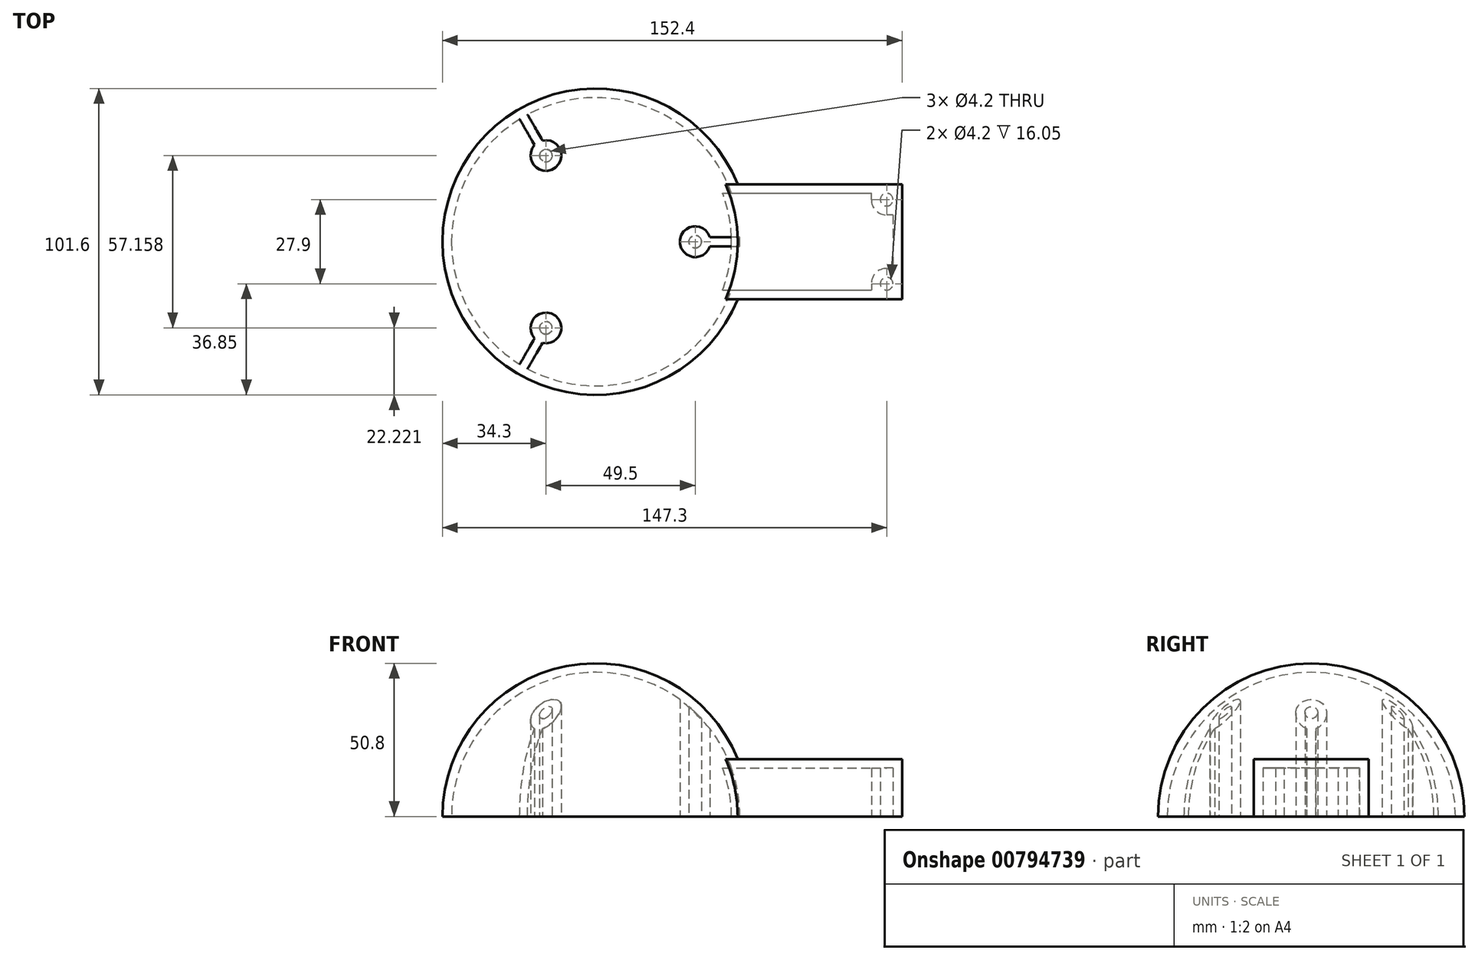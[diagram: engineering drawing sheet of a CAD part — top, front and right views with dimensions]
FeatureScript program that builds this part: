
annotation { "Feature Type Name" : "Feature", "Feature Type Description" : "" }
export const myFeature = defineFeature(function(context is Context, id is Id, definition is map)
    precondition{}
    {
        {
            var Q0;
            Q0=qCreatedBy(makeId("Top.planeOp"),FACE);
            var sketch = newSketch(context, id + "F0", { "sketchPlane" : qUnion([Q0])});
            skArc(sketch, "E0", {"start": v(25.4, 0) * mm, "mid": v(-25.4, 50.8) * mm, "end": v(-76.2, 0) * mm});
            skLineSegment(sketch, "E1", {"start": v(-76.2, 0) * mm, "end": v(25.4, 0) * mm});
            skSolve(sketch);
        }
        {
            var Q0;
            Q0 = qSketchRegion(id + "F0", true);
            var Q1;
            Q1=sQuery(id+"F0.wireOp",EDGE,"E1");
            revolve(context, id + "F1", {"surfaceOperationType" : NewSurfaceOperationType.NEW, "entities" : qUnion([Q0]), "axis" : qUnion([Q1]), "revolveType" : RevolveType.ONE_DIRECTION, "angle" : 180 * degree});
        }
        {
            var Q0;
            Q0=qCreatedBy(makeId("Top.planeOp"),FACE);
            var sketch = newSketch(context, id + "F2", { "sketchPlane" : qUnion([Q0])});
            skLineSegment(sketch, "E2.bottom", {"start": v(0, 19.05) * mm, "end": v(76.2, 19.05) * mm});
            skLineSegment(sketch, "E2.top", {"start": v(0, -19.05) * mm, "end": v(76.2, -19.05) * mm});
            skLineSegment(sketch, "E2.left", {"start": v(0, 19.05) * mm, "end": v(0, -19.05) * mm});
            skLineSegment(sketch, "E2.right", {"start": v(76.2, 19.05) * mm, "end": v(76.2, -19.05) * mm});
            skSolve(sketch);
        }
        {
            var Q0;
            Q0 = qSketchRegion(id + "F2", true);
            extrude(context, id + "F3", {"entities" : qUnion([Q0]), "operationType" : NewBodyOperationType.ADD, "depth" : 19.05 * mm, "offsetDistance" : 25.4 * mm});
        }
        {
            var Q0;
            Q0=makeQuery(id+"F3.boolean.opBoolean","MERGE",FACE,{"derivedFrom":[makeQuery(id+"F1.opRevolve","CAP_FACE",FACE,{"disambiguationData":[OSD([sQuery(id+"F0.wireOp",EDGE,"E0"),sQuery(id+"F0.wireOp",EDGE,"E1")])],"isStart":true}),makeQuery(id+"F3.opExtrude","CAP_FACE",FACE,{"disambiguationData":[OSD([sQuery(id+"F2.wireOp",EDGE,"E2.bottom"),sQuery(id+"F2.wireOp",EDGE,"E2.top"),sQuery(id+"F2.wireOp",EDGE,"E2.left"),sQuery(id+"F2.wireOp",EDGE,"E2.right")])],"isStart":true})]});
            shell(context, id + "F4", {"entities" : qUnion([Q0]), "thickness" : 3 * mm});
        }
        {
            var Q0;
            Q0=qCreatedBy(makeId("Top.planeOp"),FACE);
            var sketch = newSketch(context, id + "F5", { "sketchPlane" : qUnion([Q0])});
            skCircle(sketch, "E3", {"center": v(71.1, -13.95) * mm, "radius": 5.1 * mm, "construction": true});
            skCircle(sketch, "E4", {"center": v(71.1, -13.95) * mm, "radius": 2.1 * mm, "construction": true});
            skCircle(sketch, "E5", {"center": v(71.1, 13.95) * mm, "radius": 5.1 * mm, "construction": true});
            skCircle(sketch, "E6", {"center": v(71.1, 13.95) * mm, "radius": 2.1 * mm, "construction": true});
            skArc(sketch, "E7", {"start": v(12.47, 1.5) * mm, "mid": v(2.5, 0) * mm, "end": v(12.47, -1.5) * mm});
            skCircle(sketch, "E8", {"center": v(7.6, 0) * mm, "radius": 2.1 * mm});
            skArc(sketch, "E9", {"start": v(-43.04, -33.55) * mm, "mid": v(-39.35, -24.16) * mm, "end": v(-45.64, -32.05) * mm});
            skCircle(sketch, "E10", {"center": v(-41.9, -28.58) * mm, "radius": 2.1 * mm});
            skArc(sketch, "E11", {"start": v(-45.64, 32.05) * mm, "mid": v(-39.35, 24.16) * mm, "end": v(-43.04, 33.55) * mm});
            skCircle(sketch, "E12", {"center": v(-41.9, 28.58) * mm, "radius": 2.1 * mm});
            skLineSegment(sketch, "E13", {"start": v(-41.9, 28.58) * mm, "end": v(-41.9, -28.58) * mm, "construction": true});
            skLineSegment(sketch, "E14", {"start": v(7.6, 0) * mm, "end": v(-41.9, 28.58) * mm, "construction": true});
            skLineSegment(sketch, "E15", {"start": v(-41.9, -28.58) * mm, "end": v(7.6, 0) * mm, "construction": true});
            skCircle(sketch, "E16", {"center": v(-25.4, 0) * mm, "radius": 38.1 * mm, "construction": true});
            skLineSegment(sketch, "E17", {"start": v(-50.6, -40.65) * mm, "end": v(-45.64, -32.05) * mm});
            skLineSegment(sketch, "E18", {"start": v(-50.6, -40.65) * mm, "end": v(-48, -42.15) * mm});
            skLineSegment(sketch, "E19", {"start": v(-48, -42.15) * mm, "end": v(-43.04, -33.55) * mm});
            skLineSegment(sketch, "E20", {"start": v(-41.9, -28.58) * mm, "end": v(-25.4, 0) * mm, "construction": true});
            skLineSegment(sketch, "E21", {"start": v(-48, 42.15) * mm, "end": v(-43.04, 33.55) * mm});
            skLineSegment(sketch, "E22", {"start": v(-48, 42.15) * mm, "end": v(-50.6, 40.65) * mm});
            skLineSegment(sketch, "E23", {"start": v(-50.6, 40.65) * mm, "end": v(-45.64, 32.05) * mm});
            skLineSegment(sketch, "E24", {"start": v(-25.4, 0) * mm, "end": v(-41.9, 28.58) * mm, "construction": true});
            skLineSegment(sketch, "E25", {"start": v(12.47, -1.5) * mm, "end": v(26.65, -1.5) * mm});
            skLineSegment(sketch, "E26", {"start": v(26.65, -1.5) * mm, "end": v(26.65, 1.5) * mm});
            skLineSegment(sketch, "E27", {"start": v(26.65, 1.5) * mm, "end": v(12.47, 1.5) * mm});
            skLineSegment(sketch, "E28", {"start": v(7.6, 0) * mm, "end": v(26.65, 0) * mm, "construction": true});
            skSolve(sketch);
        }
        {
            var Q0;
            Q0 = qSketchRegion(id + "F5", true);
            var Q1;
            Q1=makeQuery(id+"F4.opShell","OFFSET_FACE",FACE,{"disambiguationData":[OSD([sQuery(id+"F0.wireOp",EDGE,"E0")])]});
            var Q2;
            Q2=makeQuery(id+"F1.opRevolve","SWEPT_BODY",BODY,{"disambiguationData":[OSD([sQuery(id+"F0.wireOp",EDGE,"E0"),sQuery(id+"F0.wireOp",EDGE,"E1")])]});
            extrude(context, id + "F6", {"entities" : qUnion([Q0]), "operationType" : NewBodyOperationType.ADD, "endBound" : BoundingType.UP_TO_SURFACE, "depth" : 25.4 * mm, "endBoundEntityFace" : qUnion([Q1]), "endBoundEntityBody" : qUnion([Q2]), "offsetDistance" : 25.4 * mm});
        }
        {
            var Q0;
            Q0=qCreatedBy(makeId("Top.planeOp"),FACE);
            var sketch = newSketch(context, id + "F7", { "sketchPlane" : qUnion([Q0])});
            skArc(sketch, "E29.0", {"start": v(71.1, -8.85) * mm, "mid": v(67.5, -10.34) * mm, "end": v(66, -13.95) * mm});
            skCircle(sketch, "E29.3", {"center": v(71.1, 13.95) * mm, "radius": 2.1 * mm});
            skLineSegment(sketch, "E30", {"start": v(66, -13.95) * mm, "end": v(66, -19.05) * mm});
            skLineSegment(sketch, "E31", {"start": v(71.1, -8.85) * mm, "end": v(76.2, -8.85) * mm});
            skCircle(sketch, "E32.0", {"center": v(71.1, -13.95) * mm, "radius": 5.1 * mm, "construction": true});
            skCircle(sketch, "E32.1", {"center": v(71.1, -13.95) * mm, "radius": 2.1 * mm});
            skArc(sketch, "E32.2", {"start": v(66, 13.95) * mm, "mid": v(67.5, 10.34) * mm, "end": v(71.1, 8.85) * mm});
            skLineSegment(sketch, "E33", {"start": v(66, -19.05) * mm, "end": v(76.2, -19.05) * mm});
            skLineSegment(sketch, "E34", {"start": v(76.2, -19.05) * mm, "end": v(76.2, -8.85) * mm});
            skLineSegment(sketch, "E35", {"start": v(66, 13.95) * mm, "end": v(66, 19.05) * mm});
            skLineSegment(sketch, "E36", {"start": v(66, 19.05) * mm, "end": v(76.2, 19.05) * mm});
            skLineSegment(sketch, "E37", {"start": v(76.2, 19.05) * mm, "end": v(76.2, 8.85) * mm});
            skLineSegment(sketch, "E38", {"start": v(76.2, 8.85) * mm, "end": v(71.1, 8.85) * mm});
            skCircle(sketch, "E39.0", {"center": v(71.1, 13.95) * mm, "radius": 5.1 * mm, "construction": true});
            skSolve(sketch);
        }
        {
            var Q0;
            Q0 = qSketchRegion(id + "F7", true);
            var Q1;
            {var subQ0=sQuery(id+"F2.wireOp",EDGE,"E2.right");var subQ1=sQuery(id+"F2.wireOp",EDGE,"E2.top");Q1=makeQuery(id+"F4.opShell","OFFSET_VERTEX",VERTEX,{"disambiguationData":[OSD([subQ1,subQ0]),TDD([makeQuery(id+"F3.opExtrude","CAP_VERTEX",VERTEX,{"disambiguationData":[OSD([subQ1,subQ0])],"isStart":false})])]});}
            extrude(context, id + "F8", {"entities" : qUnion([Q0]), "operationType" : NewBodyOperationType.ADD, "endBound" : BoundingType.UP_TO_VERTEX, "depth" : 25.4 * mm, "endBoundEntityVertex" : qUnion([Q1]), "offsetDistance" : 25.4 * mm});
        }
    });
